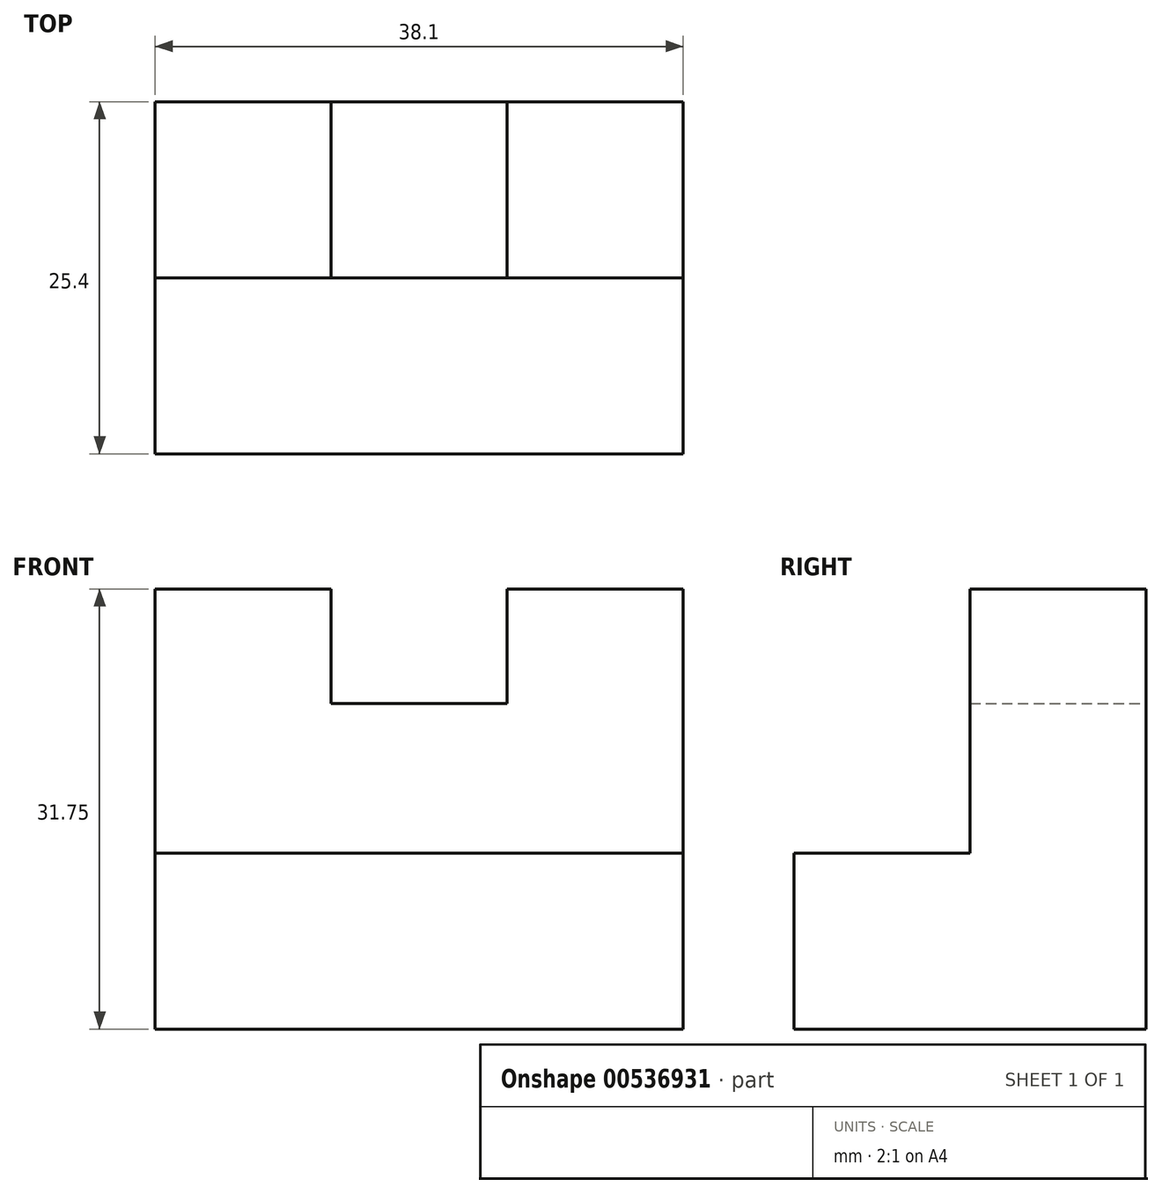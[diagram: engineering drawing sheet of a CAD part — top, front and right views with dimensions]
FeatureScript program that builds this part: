
annotation { "Feature Type Name" : "Feature", "Feature Type Description" : "" }
export const myFeature = defineFeature(function(context is Context, id is Id, definition is map)
    precondition{}
    {
        {
            var Q0;
            Q0=qCreatedBy(makeId("Front.planeOp"),FACE);
            var sketch = newSketch(context, id + "F0", { "sketchPlane" : qUnion([Q0])});
            skLineSegment(sketch, "E0", {"start": v(-43.09, 0) * mm, "end": v(-43.09, 31.75) * mm});
            skLineSegment(sketch, "E1", {"start": v(-43.09, 31.75) * mm, "end": v(-30.39, 31.75) * mm});
            skLineSegment(sketch, "E2", {"start": v(-30.39, 31.75) * mm, "end": v(-30.39, 23.49) * mm});
            skLineSegment(sketch, "E3", {"start": v(-30.39, 23.49) * mm, "end": v(-17.69, 23.49) * mm});
            skLineSegment(sketch, "E4", {"start": v(-17.69, 23.49) * mm, "end": v(-17.69, 31.75) * mm});
            skLineSegment(sketch, "E5", {"start": v(-17.69, 31.75) * mm, "end": v(-4.99, 31.75) * mm});
            skLineSegment(sketch, "E6", {"start": v(-4.99, 31.75) * mm, "end": v(-4.99, 0) * mm});
            skLineSegment(sketch, "E7", {"start": v(-4.99, 0) * mm, "end": v(-43.09, 0) * mm});
            skSolve(sketch);
        }
        {
            var Q0;
            Q0=makeQuery(id+"F0.imprint","IMPRINT",FACE,{"disambiguationData":[TD([[makeQuery(id+"F0.imprint","IMPRINT",EDGE,{"derivedFrom":sQuery(id+"F0.wireOp",EDGE,"E0")}),-1.0]])]});
            extrude(context, id + "F1", {"entities" : qUnion([Q0]), "depth" : 12.7 * mm, "offsetDistance" : 25.4 * mm});
        }
        {
            var Q0;
            Q0=makeQuery(id+"F1.opExtrude","CAP_FACE",FACE,{"disambiguationData":[OSD([sQuery(id+"F0.wireOp",EDGE,"E0"),sQuery(id+"F0.wireOp",EDGE,"E1"),sQuery(id+"F0.wireOp",EDGE,"E2"),sQuery(id+"F0.wireOp",EDGE,"E3"),sQuery(id+"F0.wireOp",EDGE,"E4"),sQuery(id+"F0.wireOp",EDGE,"E5"),sQuery(id+"F0.wireOp",EDGE,"E6"),sQuery(id+"F0.wireOp",EDGE,"E7")])],"isStart":false});
            var sketch = newSketch(context, id + "F2", { "sketchPlane" : qUnion([Q0])});
            skLineSegment(sketch, "E8", {"start": v(-43.09, 0) * mm, "end": v(-43.09, 12.7) * mm});
            skLineSegment(sketch, "E9", {"start": v(-43.09, 12.7) * mm, "end": v(-4.99, 12.7) * mm});
            skLineSegment(sketch, "E10", {"start": v(-4.99, 12.7) * mm, "end": v(-4.99, 0) * mm});
            skLineSegment(sketch, "E11", {"start": v(-4.99, 0) * mm, "end": v(-43.09, 0) * mm});
            skSolve(sketch);
        }
        {
            var Q0;
            Q0 = qSketchRegion(id + "F2", true);
            extrude(context, id + "F3", {"entities" : qUnion([Q0]), "operationType" : NewBodyOperationType.ADD, "depth" : 12.7 * mm, "offsetDistance" : 25.4 * mm});
        }
    });
